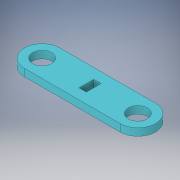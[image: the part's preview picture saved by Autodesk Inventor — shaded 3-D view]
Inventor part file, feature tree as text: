
AUTODESK INVENTOR PART (.ipt)
format: ipt  version: 2017 (Build 210142000, 142)  size: 118,272 bytes
history: native  units: in
note: dims shown in document units (in); Inventor stores cm internally (conversion verified against a paired STEP export)
features: extrude x1, sketch x1
ambient origin geometry x8: Origin, YZ Plane, XZ Plane, XY Plane, X Axis, Y Axis, Z Axis, Center Point
bodies: Body1 (feature_tree)
feature tree (2):
  extrude  "Extrusion2"  Depth=0.9449in
  sketch  "Sketch1"  dims[d0=2.5591in d1=0.9449in d2=0.5118in d8=0.1969in d9=0.0in d11=0.1969in d12=0.3937in]
